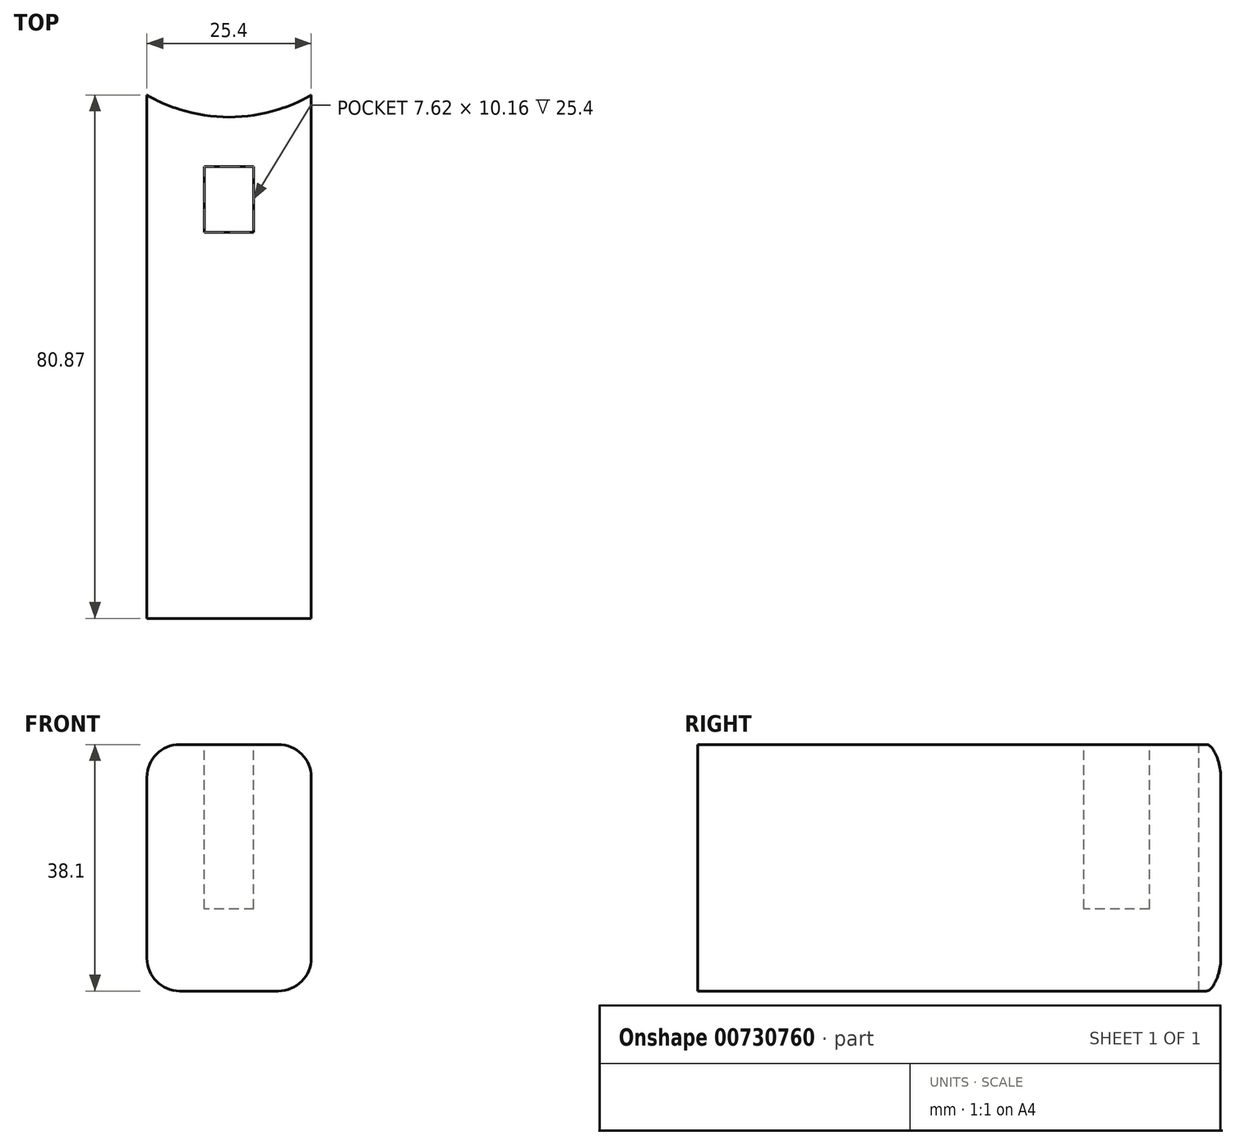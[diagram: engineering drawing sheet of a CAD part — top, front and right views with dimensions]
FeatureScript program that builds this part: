
annotation { "Feature Type Name" : "Feature", "Feature Type Description" : "" }
export const myFeature = defineFeature(function(context is Context, id is Id, definition is map)
    precondition{}
    {
        {
            var Q0;
            Q0=qCreatedBy(makeId("Top.planeOp"),FACE);
            var sketch = newSketch(context, id + "F0", { "sketchPlane" : qUnion([Q0])});
            skLineSegment(sketch, "E0", {"start": v(0, 0) * mm, "end": v(0, -82.55) * mm});
            skLineSegment(sketch, "E1", {"start": v(0, -82.55) * mm, "end": v(25.4, -82.55) * mm});
            skLineSegment(sketch, "E2", {"start": v(25.4, -82.55) * mm, "end": v(25.4, 0) * mm});
            skLineSegment(sketch, "E3", {"start": v(25.4, 0) * mm, "end": v(0, 0) * mm});
            skSolve(sketch);
        }
        {
            var Q0;
            Q0=makeQuery(id+"F0.imprint","IMPRINT",FACE,{"disambiguationData":[TD([[makeQuery(id+"F0.imprint","IMPRINT",EDGE,{"derivedFrom":sQuery(id+"F0.wireOp",EDGE,"E0")}),1.0]])]});
            extrude(context, id + "F1", {"entities" : qUnion([Q0]), "depth" : 38.1 * mm, "offsetDistance" : 25.4 * mm});
        }
        {
            var Q0;
            Q0=makeQuery(id+"F1.opExtrude","CAP_FACE",FACE,{"disambiguationData":[OSD([sQuery(id+"F0.wireOp",EDGE,"E0"),sQuery(id+"F0.wireOp",EDGE,"E1"),sQuery(id+"F0.wireOp",EDGE,"E2"),sQuery(id+"F0.wireOp",EDGE,"E3")])],"isStart":false});
            var sketch = newSketch(context, id + "F2", { "sketchPlane" : qUnion([Q0])});
            skCircle(sketch, "E4", {"center": v(12.7, 20.32) * mm, "radius": 25.4 * mm});
            skSolve(sketch);
        }
        {
            var Q0;
            {var subQ5=makeQuery(id+"F1.opExtrude","CAP_EDGE",EDGE,{"disambiguationData":[OSD([sQuery(id+"F0.wireOp",EDGE,"E3")])],"isStart":false});Q0=makeQuery(id+"F2.imprint","IMPRINT",FACE,{"disambiguationData":[TD([[makeQuery(id+"F2.imprint","IMPRINT",EDGE,{"derivedFrom":subQ5}),-1.0]])]});}
            var Q1;
            {var subQ5=makeQuery(id+"F1.opExtrude","CAP_EDGE",EDGE,{"disambiguationData":[OSD([sQuery(id+"F0.wireOp",EDGE,"E3")])],"isStart":false});Q1=makeQuery(id+"F2.imprint","IMPRINT",FACE,{"disambiguationData":[TD([[makeQuery(id+"F2.imprint","IMPRINT",EDGE,{"derivedFrom":subQ5}),1.0]])]});}
            extrude(context, id + "F3", {"entities" : qUnion([Q0, Q1]), "operationType" : NewBodyOperationType.REMOVE, "oppositeDirection" : true, "depth" : 76.2 * mm, "offsetDistance" : 25.4 * mm});
        }
        {
            var Q0;
            Q0=makeQuery(id+"F1.opExtrude","CAP_FACE",FACE,{"disambiguationData":[OSD([sQuery(id+"F0.wireOp",EDGE,"E0"),sQuery(id+"F0.wireOp",EDGE,"E1"),sQuery(id+"F0.wireOp",EDGE,"E2"),sQuery(id+"F0.wireOp",EDGE,"E3")])],"isStart":false});
            var sketch = newSketch(context, id + "F4", { "sketchPlane" : qUnion([Q0])});
            skLineSegment(sketch, "E5", {"start": v(8.9, -12.7) * mm, "end": v(8.9, -22.86) * mm});
            skLineSegment(sketch, "E6", {"start": v(8.9, -22.86) * mm, "end": v(16.51, -22.86) * mm});
            skLineSegment(sketch, "E7", {"start": v(16.51, -22.86) * mm, "end": v(16.51, -12.7) * mm});
            skLineSegment(sketch, "E8", {"start": v(16.51, -12.7) * mm, "end": v(8.9, -12.7) * mm});
            skSolve(sketch);
        }
        {
            var Q0;
            Q0=makeQuery(id+"F4.imprint","IMPRINT",FACE,{"disambiguationData":[TD([[makeQuery(id+"F4.imprint","IMPRINT",EDGE,{"derivedFrom":sQuery(id+"F4.wireOp",EDGE,"E5")}),1.0]])]});
            extrude(context, id + "F5", {"entities" : qUnion([Q0]), "operationType" : NewBodyOperationType.REMOVE, "oppositeDirection" : true, "depth" : 25.4 * mm, "offsetDistance" : 25.4 * mm});
        }
        {
            var Q0;
            Q0=makeQuery(id+"F1.opExtrude","CAP_EDGE",EDGE,{"disambiguationData":[OSD([sQuery(id+"F0.wireOp",EDGE,"E0")])],"isStart":false});
            var Q1;
            Q1=makeQuery(id+"F1.opExtrude","CAP_EDGE",EDGE,{"disambiguationData":[OSD([sQuery(id+"F0.wireOp",EDGE,"E0")])],"isStart":true});
            var Q2;
            Q2=makeQuery(id+"F1.opExtrude","CAP_EDGE",EDGE,{"disambiguationData":[OSD([sQuery(id+"F0.wireOp",EDGE,"E2")])],"isStart":false});
            var Q3;
            Q3=makeQuery(id+"F1.opExtrude","CAP_EDGE",EDGE,{"disambiguationData":[OSD([sQuery(id+"F0.wireOp",EDGE,"E2")])],"isStart":true});
            fillet(context, id + "F6", {"entities" : qUnion([Q0, Q1, Q2, Q3]), "radius" : 5.08 * mm, "tangentPropagation" : true, "allowEdgeOverflow" : false});
        }
    });
